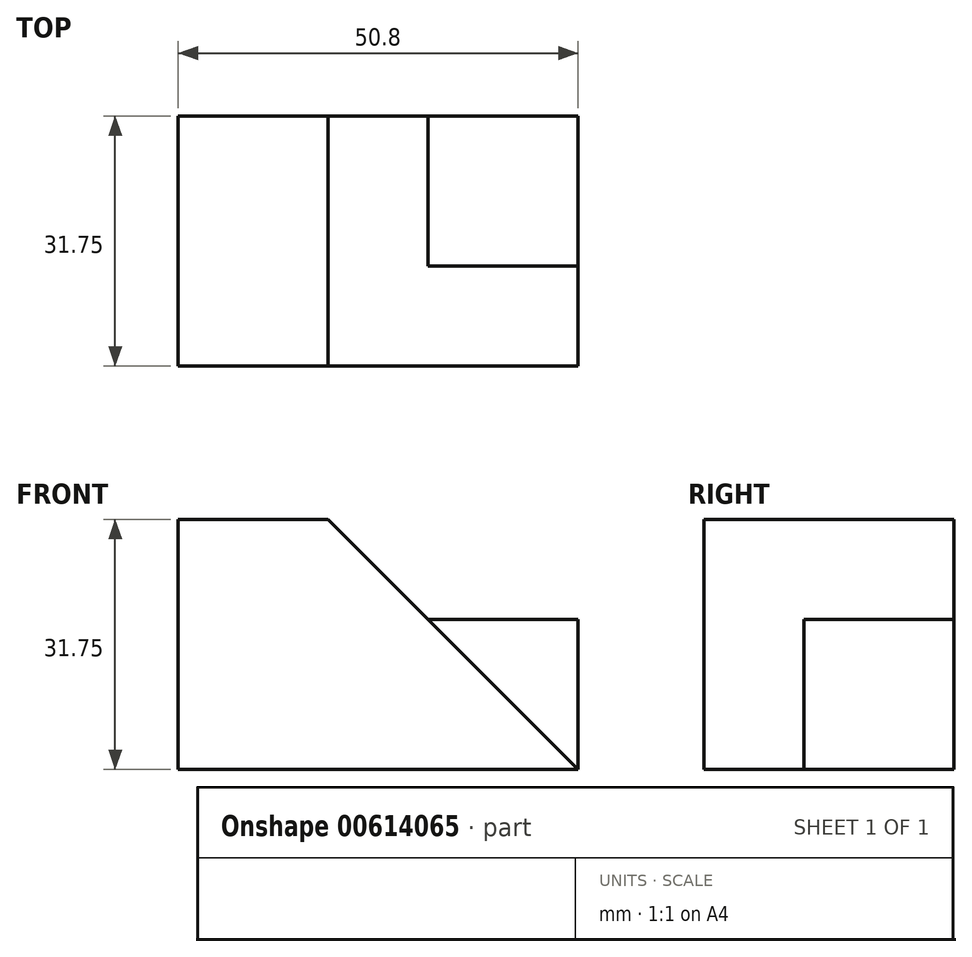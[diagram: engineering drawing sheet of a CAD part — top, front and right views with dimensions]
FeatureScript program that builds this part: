
annotation { "Feature Type Name" : "Feature", "Feature Type Description" : "" }
export const myFeature = defineFeature(function(context is Context, id is Id, definition is map)
    precondition{}
    {
        {
            var Q0;
            Q0=qCreatedBy(makeId("Front.planeOp"),FACE);
            var sketch = newSketch(context, id + "F0", { "sketchPlane" : qUnion([Q0])});
            skLineSegment(sketch, "E0", {"start": v(0, 0) * mm, "end": v(50.8, 0) * mm});
            skLineSegment(sketch, "E1", {"start": v(50.8, 0) * mm, "end": v(19.05, 31.75) * mm});
            skLineSegment(sketch, "E2", {"start": v(19.05, 31.75) * mm, "end": v(0, 31.75) * mm});
            skLineSegment(sketch, "E3", {"start": v(0, 31.75) * mm, "end": v(0, 0) * mm});
            skSolve(sketch);
        }
        {
            var Q0;
            Q0 = qSketchRegion(id + "F0", true);
            extrude(context, id + "F1", {"entities" : qUnion([Q0]), "depth" : 31.75 * mm, "offsetDistance" : 25.4 * mm});
        }
        {
            var Q0;
            Q0=makeQuery(id+"F1.opExtrude","CAP_FACE",FACE,{"disambiguationData":[OSD([sQuery(id+"F0.wireOp",EDGE,"E0"),sQuery(id+"F0.wireOp",EDGE,"E1"),sQuery(id+"F0.wireOp",EDGE,"E2"),sQuery(id+"F0.wireOp",EDGE,"E3")])],"isStart":true});
            var sketch = newSketch(context, id + "F2", { "sketchPlane" : qUnion([Q0])});
            skLineSegment(sketch, "E4", {"start": v(-50.8, 0) * mm, "end": v(-50.8, 19.05) * mm});
            skLineSegment(sketch, "E5", {"start": v(-50.8, 19.05) * mm, "end": v(-31.75, 19.05) * mm});
            skLineSegment(sketch, "E6", {"start": v(-50.8, 0) * mm, "end": v(-31.75, 19.05) * mm});
            skSolve(sketch);
        }
        {
            var Q0;
            Q0 = qSketchRegion(id + "F2", true);
            extrude(context, id + "F3", {"entities" : qUnion([Q0]), "operationType" : NewBodyOperationType.ADD, "oppositeDirection" : true, "depth" : 19.05 * mm, "offsetDistance" : 25.4 * mm});
        }
    });
